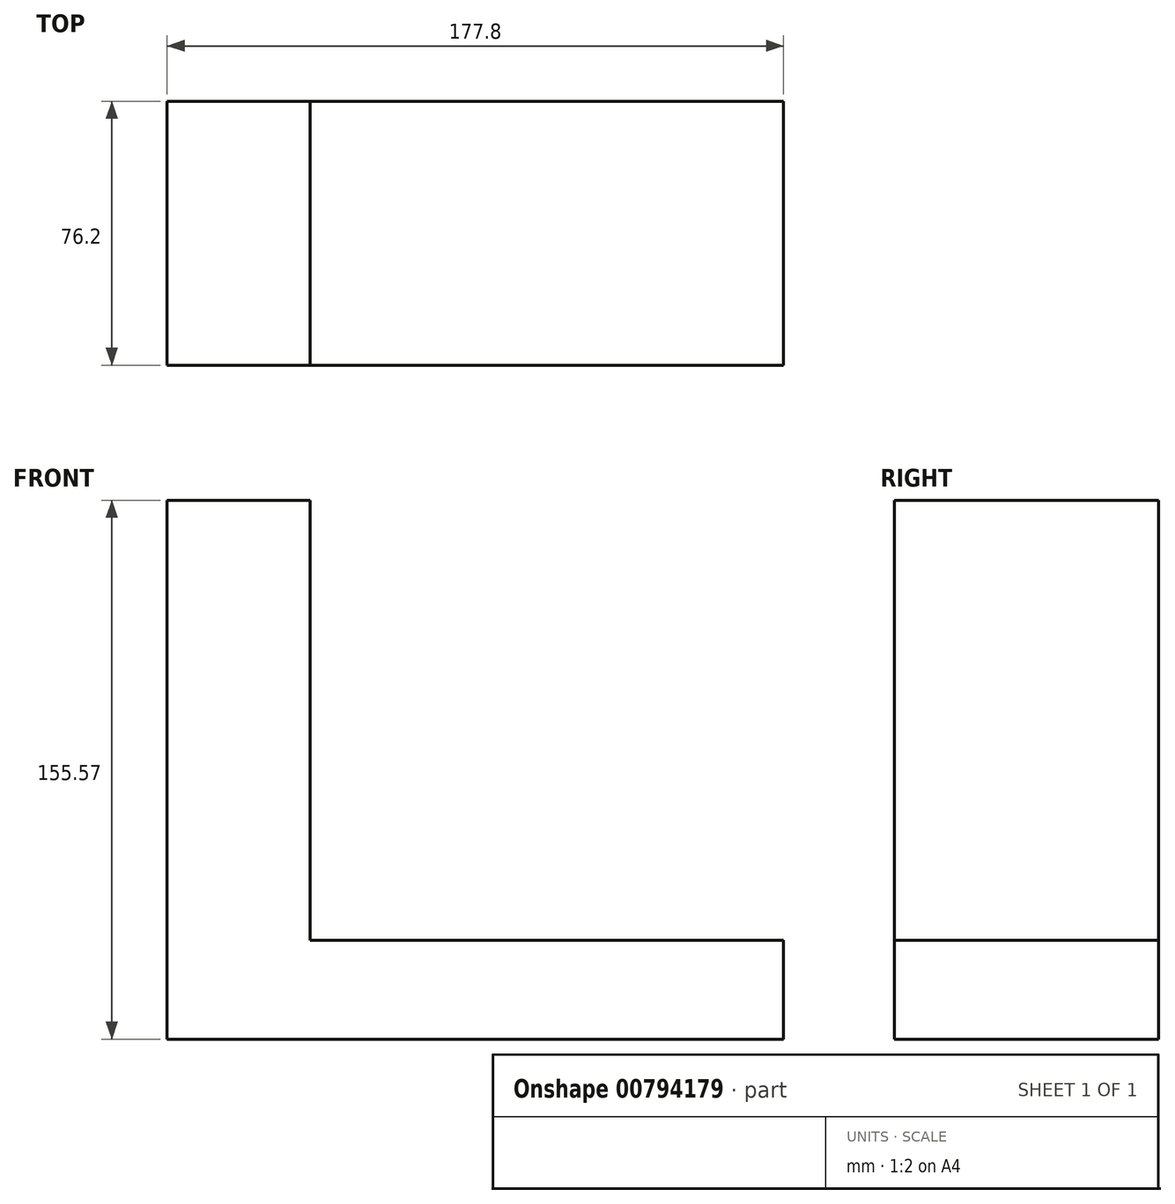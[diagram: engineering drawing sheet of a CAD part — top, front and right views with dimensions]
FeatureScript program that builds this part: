
annotation { "Feature Type Name" : "Feature", "Feature Type Description" : "" }
export const myFeature = defineFeature(function(context is Context, id is Id, definition is map)
    precondition{}
    {
        {
            var Q0;
            Q0=qCreatedBy(makeId("Front.planeOp"),FACE);
            var sketch = newSketch(context, id + "F0", { "sketchPlane" : qUnion([Q0])});
            skLineSegment(sketch, "E0", {"start": v(0, 0) * mm, "end": v(177.8, 0) * mm});
            skLineSegment(sketch, "E1", {"start": v(177.8, 0) * mm, "end": v(177.8, 28.58) * mm});
            skLineSegment(sketch, "E2", {"start": v(177.8, 28.58) * mm, "end": v(41.28, 28.58) * mm});
            skLineSegment(sketch, "E3", {"start": v(41.28, 28.58) * mm, "end": v(41.28, 155.57) * mm});
            skLineSegment(sketch, "E4", {"start": v(41.28, 155.57) * mm, "end": v(0, 155.57) * mm});
            skLineSegment(sketch, "E5", {"start": v(0, 155.57) * mm, "end": v(0, 0) * mm});
            skSolve(sketch);
        }
        {
            var Q0;
            Q0 = qSketchRegion(id + "F0", true);
            extrude(context, id + "F1", {"entities" : qUnion([Q0]), "oppositeDirection" : true, "depth" : 76.2 * mm, "offsetDistance" : 25.4 * mm});
        }
    });
